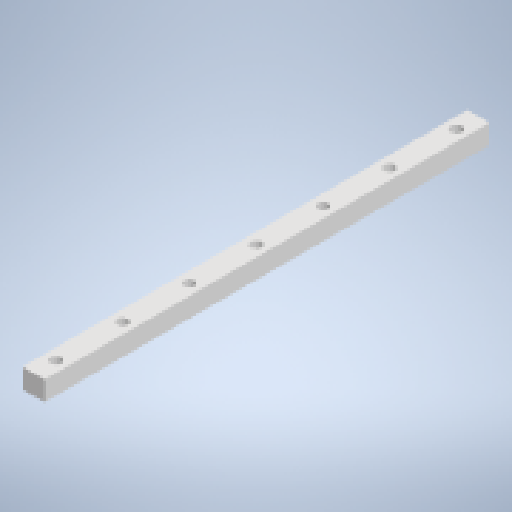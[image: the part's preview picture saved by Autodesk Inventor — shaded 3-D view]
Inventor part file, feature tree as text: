
AUTODESK INVENTOR PART (.ipt)
format: ipt  version: 2025.2 (Build 292293000, 293)  size: 146,944 bytes
history: native  units: mm
features: extrude x3, pattern_linear x1
ambient origin geometry x8: Origin, YZ Plane, XZ Plane, XY Plane, X Axis, Y Axis, Z Axis, Center Point
bodies: Solid1 (feature_tree)
feature tree (4):
  extrude  "Extrusion1"  Depth=20.0mm
  extrude  "Extrusion2"  Depth=17.5mm
  extrude  "Extrusion3"  Depth=400.0mm TaperAngle=0.0deg
  pattern_linear  "Rectangular Pattern1"  Spacing1=6.0mm  [1 undecoded]
note: 1 required parameter value undecoded (feature->parameter linkage not recoverable at this tier; creation-order binding heuristic only, values carry confidence <= 0.55)
